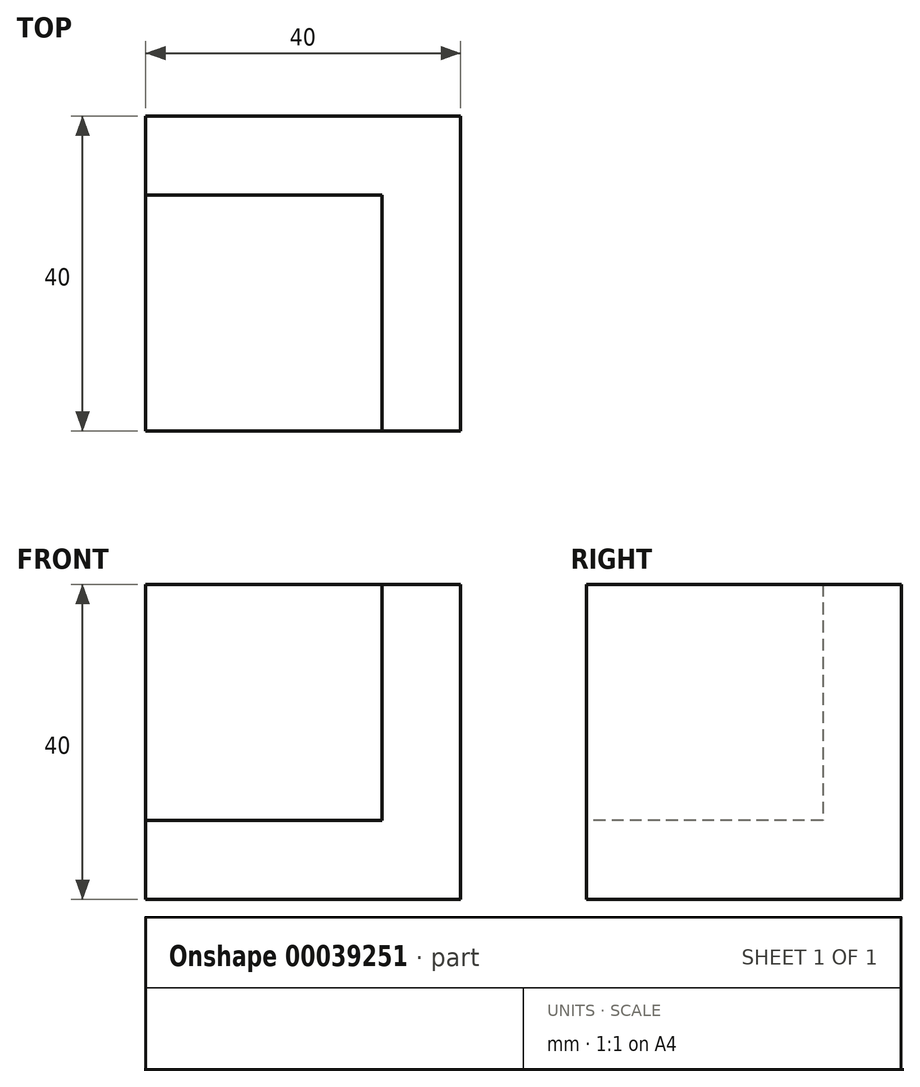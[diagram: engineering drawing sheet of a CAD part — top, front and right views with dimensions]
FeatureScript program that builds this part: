
annotation { "Feature Type Name" : "Feature", "Feature Type Description" : "" }
export const myFeature = defineFeature(function(context is Context, id is Id, definition is map)
    precondition{}
    {
        {
            var Q0;
            Q0=qCreatedBy(makeId("Front.planeOp"),FACE);
            var sketch = newSketch(context, id + "F0", { "sketchPlane" : qUnion([Q0])});
            skLineSegment(sketch, "E0.bottom", {"start": v(-56.5, 46.7) * mm, "end": v(-16.5, 46.7) * mm});
            skLineSegment(sketch, "E0.top", {"start": v(-56.5, 6.7) * mm, "end": v(-16.5, 6.7) * mm});
            skLineSegment(sketch, "E0.left", {"start": v(-56.5, 46.7) * mm, "end": v(-56.5, 6.7) * mm});
            skLineSegment(sketch, "E0.right", {"start": v(-16.5, 46.7) * mm, "end": v(-16.5, 6.7) * mm});
            skSolve(sketch);
        }
        {
            var Q0;
            Q0=makeQuery(id+"F0.imprint","IMPRINT",FACE,{"disambiguationData":[TD([[makeQuery(id+"F0.imprint","IMPRINT",EDGE,{"derivedFrom":sQuery(id+"F0.wireOp",EDGE,"E0.bottom")}),-1.0]])]});
            extrude(context, id + "F1", {"entities" : qUnion([Q0]), "depth" : 40 * mm});
        }
        {
            var Q0;
            Q0=makeQuery(id+"F1.opExtrude","CAP_FACE",FACE,{"disambiguationData":[OSD([sQuery(id+"F0.wireOp",EDGE,"E0.bottom"),sQuery(id+"F0.wireOp",EDGE,"E0.top"),sQuery(id+"F0.wireOp",EDGE,"E0.left"),sQuery(id+"F0.wireOp",EDGE,"E0.right")])],"isStart":false});
            var sketch = newSketch(context, id + "F2", { "sketchPlane" : qUnion([Q0])});
            skLineSegment(sketch, "E1.bottom", {"start": v(-56.5, 46.7) * mm, "end": v(-26.5, 46.7) * mm});
            skLineSegment(sketch, "E1.top", {"start": v(-56.5, 16.7) * mm, "end": v(-26.5, 16.7) * mm});
            skLineSegment(sketch, "E1.left", {"start": v(-56.5, 46.7) * mm, "end": v(-56.5, 16.7) * mm});
            skLineSegment(sketch, "E1.right", {"start": v(-26.5, 46.7) * mm, "end": v(-26.5, 16.7) * mm});
            skSolve(sketch);
        }
        {
            var Q0;
            Q0=makeQuery(id+"F2.imprint","IMPRINT",FACE,{"disambiguationData":[TD([[makeQuery(id+"F2.imprint","IMPRINT",EDGE,{"derivedFrom":sQuery(id+"F2.wireOp",EDGE,"E1.bottom")}),-1.0]])]});
            extrude(context, id + "F3", {"entities" : qUnion([Q0]), "operationType" : NewBodyOperationType.REMOVE, "oppositeDirection" : true, "depth" : 30 * mm});
        }
    });
